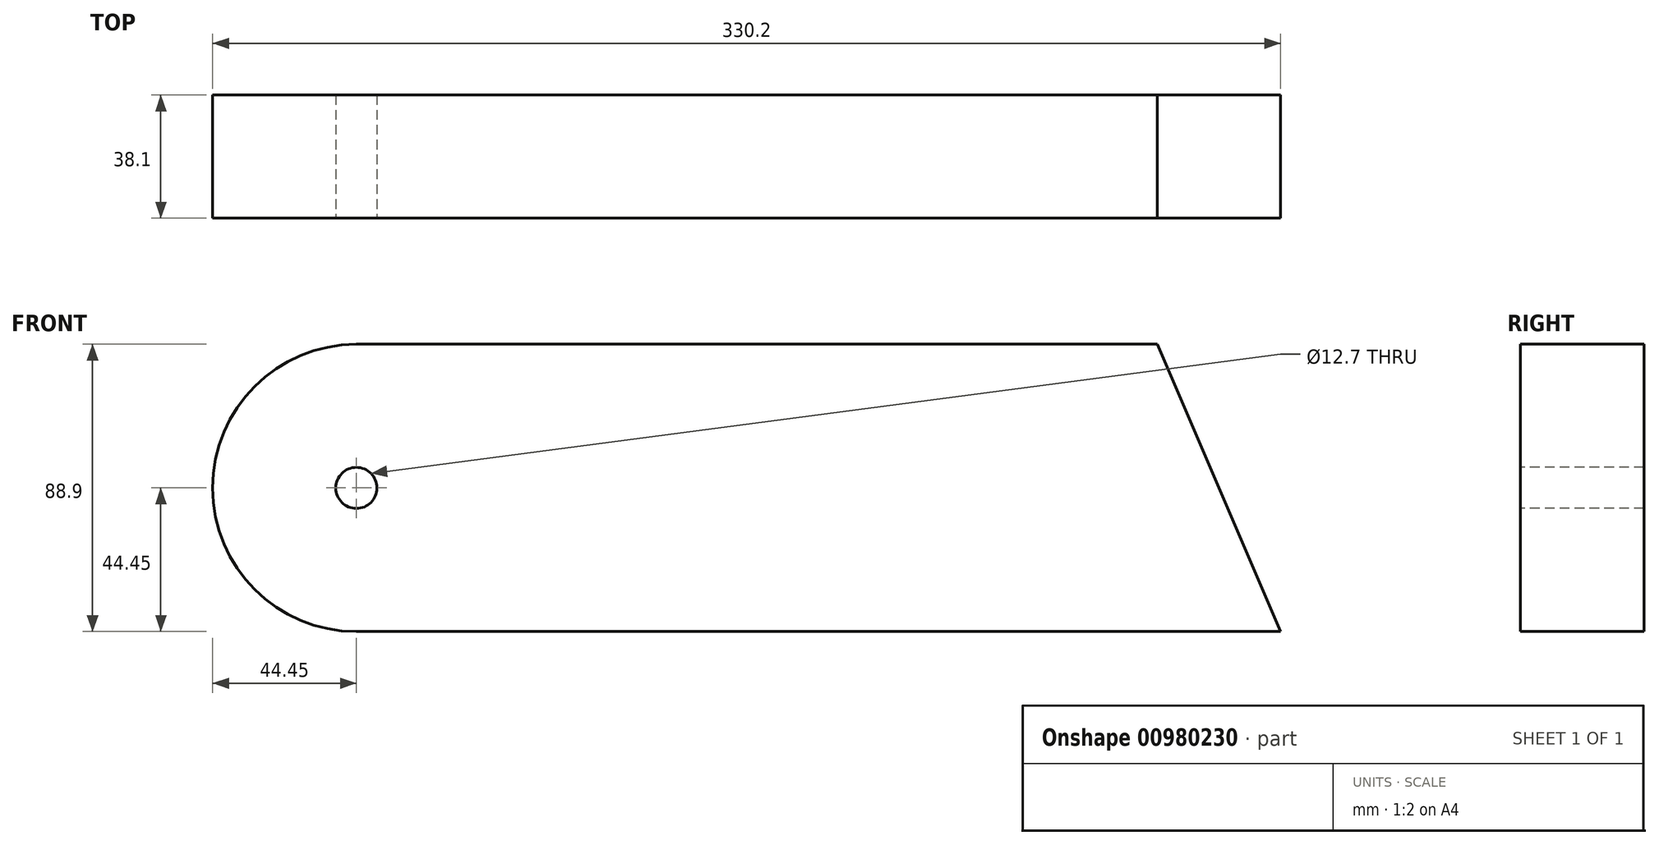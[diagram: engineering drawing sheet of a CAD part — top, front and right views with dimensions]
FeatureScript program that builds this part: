
annotation { "Feature Type Name" : "Feature", "Feature Type Description" : "" }
export const myFeature = defineFeature(function(context is Context, id is Id, definition is map)
    precondition{}
    {
        {
            var Q0;
            Q0=qCreatedBy(makeId("Right.planeOp"),FACE);
            var sketch = newSketch(context, id + "F0", { "sketchPlane" : qUnion([Q0])});
            skLineSegment(sketch, "E0.bottom", {"start": v(-19.05, -44.45) * mm, "end": v(19.05, -44.45) * mm});
            skLineSegment(sketch, "E0.top", {"start": v(-19.05, 44.45) * mm, "end": v(19.05, 44.45) * mm});
            skLineSegment(sketch, "E0.left", {"start": v(-19.05, -44.45) * mm, "end": v(-19.05, 44.45) * mm});
            skLineSegment(sketch, "E0.right", {"start": v(19.05, -44.45) * mm, "end": v(19.05, 44.45) * mm});
            skPoint(sketch, "E0.middle", {"position": v(0, 0) * mm});
            skSolve(sketch);
        }
        {
            var Q0;
            Q0=makeQuery(id+"F0.imprint","IMPRINT",FACE,{"disambiguationData":[TD([[makeQuery(id+"F0.imprint","IMPRINT",EDGE,{"derivedFrom":sQuery(id+"F0.wireOp",EDGE,"E0.bottom")}),1.0]])]});
            extrude(context, id + "F1", {"entities" : qUnion([Q0]), "oppositeDirection" : true, "depth" : 330.2 * mm, "offsetDistance" : 25.4 * mm});
        }
        {
            var Q0;
            Q0=makeQuery(id+"F1.opExtrude","SWEPT_FACE",FACE,{"disambiguationData":[OSD([sQuery(id+"F0.wireOp",EDGE,"E0.left")])]});
            var sketch = newSketch(context, id + "F2", { "sketchPlane" : qUnion([Q0])});
            skLineSegment(sketch, "E1", {"start": v(-330.2, 0) * mm, "end": v(-285.75, 0) * mm, "construction": true});
            skCircle(sketch, "E2", {"center": v(-285.75, 0) * mm, "radius": 44.45 * mm});
            skSolve(sketch);
        }
        {
            var Q0;
            {var subQ0=sQuery(id+"F2.wireOp",EDGE,"E2");var subQ1=sQuery(id+"F0.wireOp",EDGE,"E0.left");var subQ2=makeQuery(id+"F1.opExtrude","CAP_EDGE",EDGE,{"disambiguationData":[OSD([subQ1])],"isStart":false});var subQ3=makeQuery(id+"F2.imprint","INTERSECT",VERTEX,{"derivedFrom":[subQ2,subQ0]});Q0=makeQuery(id+"F2.imprint","IMPRINT",FACE,{"disambiguationData":[TD([[makeQuery(id+"F2.imprint","IMPRINT",EDGE,{"disambiguationData":[TD([[subQ3,1.0]])],"derivedFrom":subQ0}),-1.0]])]});}
            var sketch = newSketch(context, id + "F3", { "sketchPlane" : qUnion([Q0])});
            skArc(sketch, "E3.0.0", {"start": v(-330.2, 0) * mm, "mid": v(-317.18, 31.43) * mm, "end": v(-285.75, 44.45) * mm});
            skLineSegment(sketch, "E3.0.1", {"start": v(-285.75, 44.45) * mm, "end": v(-330.2, 44.45) * mm});
            skLineSegment(sketch, "E3.0.2", {"start": v(-330.2, 44.45) * mm, "end": v(-330.2, 0) * mm});
            skSolve(sketch);
        }
        {
            var Q0;
            Q0 = qSketchRegion(id + "F3", true);
            extrude(context, id + "F4", {"entities" : qUnion([Q0]), "operationType" : NewBodyOperationType.REMOVE, "oppositeDirection" : true, "depth" : 76.2 * mm, "offsetDistance" : 25.4 * mm});
        }
        {
            var Q0;
            {var subQ0=sQuery(id+"F2.wireOp",EDGE,"E2");var subQ1=sQuery(id+"F0.wireOp",EDGE,"E0.left");var subQ2=makeQuery(id+"F1.opExtrude","CAP_EDGE",EDGE,{"disambiguationData":[OSD([subQ1])],"isStart":false});var subQ3=makeQuery(id+"F2.imprint","INTERSECT",VERTEX,{"derivedFrom":[subQ2,subQ0]});Q0=makeQuery(id+"F2.imprint","IMPRINT",FACE,{"disambiguationData":[TD([[makeQuery(id+"F2.imprint","IMPRINT",EDGE,{"disambiguationData":[TD([[subQ3,-1.0]])],"derivedFrom":subQ0}),-1.0]])]});}
            extrude(context, id + "F5", {"entities" : qUnion([Q0]), "operationType" : NewBodyOperationType.REMOVE, "oppositeDirection" : true, "depth" : 76.2 * mm, "offsetDistance" : 25.4 * mm});
        }
        {
            var Q0;
            Q0=makeQuery(id+"F1.opExtrude","SWEPT_FACE",FACE,{"disambiguationData":[OSD([sQuery(id+"F0.wireOp",EDGE,"E0.left")])]});
            var sketch = newSketch(context, id + "F6", { "sketchPlane" : qUnion([Q0])});
            skLineSegment(sketch, "E4", {"start": v(-330.2, 0) * mm, "end": v(-285.75, 0) * mm, "construction": true});
            skCircle(sketch, "E5", {"center": v(-285.75, 0) * mm, "radius": 6.35 * mm});
            skSolve(sketch);
        }
        {
            var Q0;
            Q0 = qSketchRegion(id + "F6", true);
            extrude(context, id + "F7", {"entities" : qUnion([Q0]), "operationType" : NewBodyOperationType.REMOVE, "endBound" : BoundingType.THROUGH_ALL, "oppositeDirection" : true, "depth" : 25.4 * mm, "offsetDistance" : 25.4 * mm});
        }
        {
            var Q0;
            Q0=makeQuery(id+"F1.opExtrude","SWEPT_FACE",FACE,{"disambiguationData":[OSD([sQuery(id+"F0.wireOp",EDGE,"E0.left")])]});
            var sketch = newSketch(context, id + "F8", { "sketchPlane" : qUnion([Q0])});
            skLineSegment(sketch, "E6", {"start": v(-38.1, 44.45) * mm, "end": v(0, -44.45) * mm});
            skLineSegment(sketch, "E7", {"start": v(-38.1, 44.45) * mm, "end": v(0, 44.45) * mm});
            skLineSegment(sketch, "E8", {"start": v(0, 44.45) * mm, "end": v(0, -44.45) * mm});
            skSolve(sketch);
        }
        {
            var Q0;
            Q0=makeQuery(id+"F8.imprint","IMPRINT",FACE,{"disambiguationData":[TD([[makeQuery(id+"F8.imprint","IMPRINT",EDGE,{"derivedFrom":sQuery(id+"F8.wireOp",EDGE,"E6")}),1.0]])]});
            extrude(context, id + "F9", {"entities" : qUnion([Q0]), "operationType" : NewBodyOperationType.REMOVE, "oppositeDirection" : true, "depth" : 50.8 * mm, "offsetDistance" : 25.4 * mm});
        }
    });
